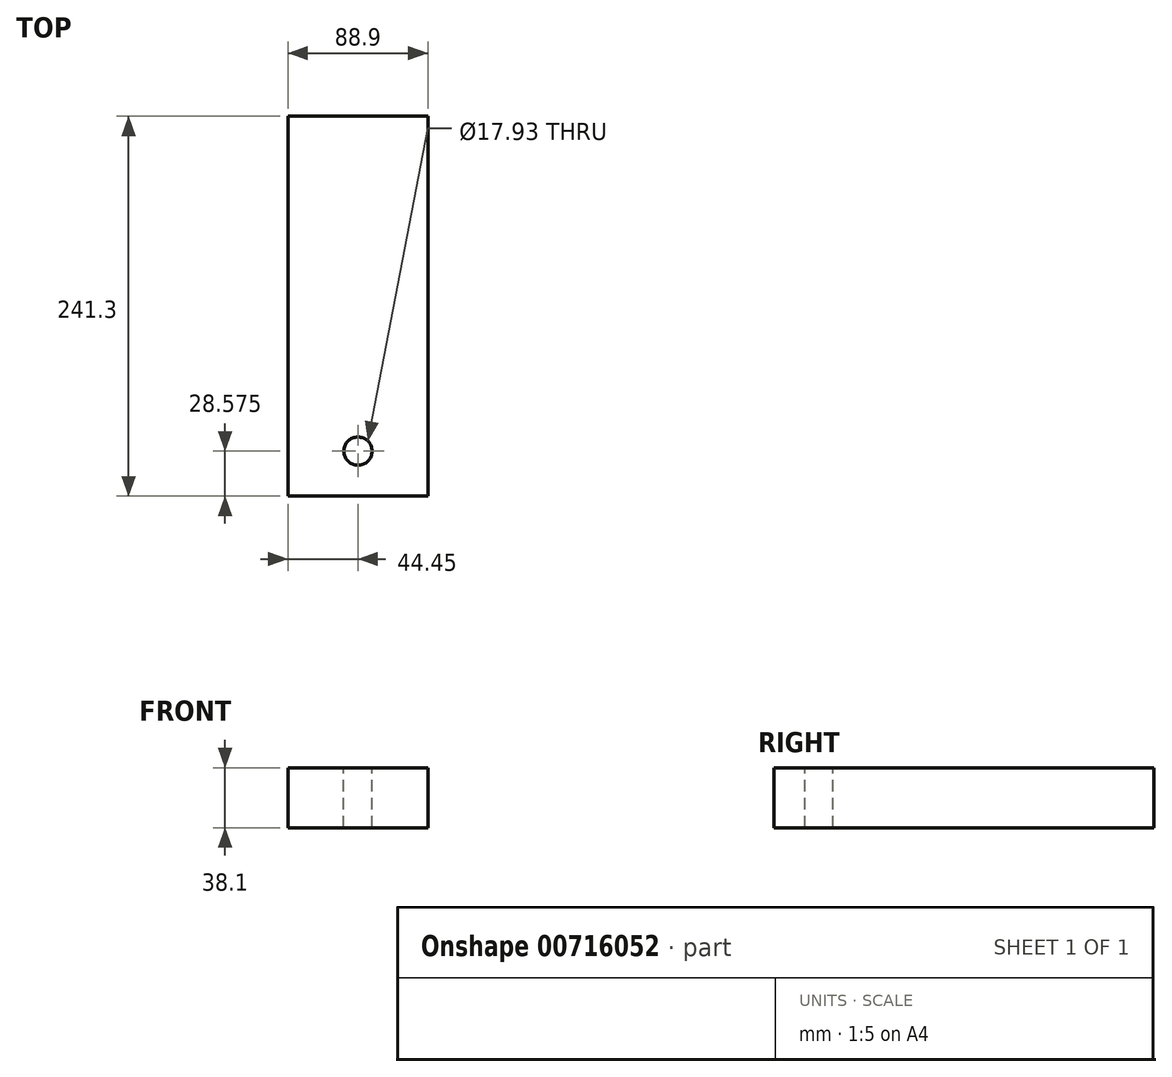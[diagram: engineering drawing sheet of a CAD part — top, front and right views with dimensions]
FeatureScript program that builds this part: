
annotation { "Feature Type Name" : "Feature", "Feature Type Description" : "" }
export const myFeature = defineFeature(function(context is Context, id is Id, definition is map)
    precondition{}
    {
        {
            var Q0;
            Q0=qCreatedBy(makeId("Front.planeOp"),FACE);
            var sketch = newSketch(context, id + "F0", { "sketchPlane" : qUnion([Q0])});
            skLineSegment(sketch, "E0.bottom", {"start": v(-44.45, 19.05) * mm, "end": v(44.45, 19.05) * mm});
            skLineSegment(sketch, "E0.top", {"start": v(-44.45, -19.05) * mm, "end": v(44.45, -19.05) * mm});
            skLineSegment(sketch, "E0.left", {"start": v(-44.45, 19.05) * mm, "end": v(-44.45, -19.05) * mm});
            skLineSegment(sketch, "E0.right", {"start": v(44.45, 19.05) * mm, "end": v(44.45, -19.05) * mm});
            skLineSegment(sketch, "E1", {"start": v(0, 0) * mm, "end": v(110.39, 0) * mm, "construction": true});
            skLineSegment(sketch, "E2", {"start": v(0, 0) * mm, "end": v(0, 61.99) * mm, "construction": true});
            skSolve(sketch);
        }
        {
            var Q0;
            Q0 = qSketchRegion(id + "F0", true);
            extrude(context, id + "F1", {"entities" : qUnion([Q0]), "depth" : 241.3 * mm, "offsetDistance" : 25.4 * mm});
        }
        {
            var Q0;
            Q0=makeQuery(id+"F1.opExtrude","SWEPT_FACE",FACE,{"disambiguationData":[OSD([sQuery(id+"F0.wireOp",EDGE,"E0.bottom")])]});
            var sketch = newSketch(context, id + "F2", { "sketchPlane" : qUnion([Q0])});
            skCircle(sketch, "E3", {"center": v(0, -212.73) * mm, "radius": 8.97 * mm});
            skSolve(sketch);
        }
        {
            var Q0;
            Q0 = qSketchRegion(id + "F2", true);
            extrude(context, id + "F3", {"entities" : qUnion([Q0]), "operationType" : NewBodyOperationType.REMOVE, "oppositeDirection" : true, "depth" : 38.1 * mm, "offsetDistance" : 25.4 * mm});
        }
    });
